# Revit family: 07101_CAI
name_source: partatom
category: Air Terminals
revit_build: Autodesk Revit MEP 2012 (Build: 20110309_2315(x64)
units: mm (PartAtom-declared; Revit-internal decimal feet)

## types (8) — shared parameters
Conect_Horizontal = 23 7/8"
Description = Difusor lineal para inyección
Función = Inyección
Longitud Mín.-Máx. = 24" (0.61 m) a 157 1/2" (4.0 m) en una sola pieza.
Manufacturer = INNES
Material = Aluminio
Medida_Requerida = 24"
Model = CAI
Nota1 = .
Nota_2 = .
Nota_3 = .
Posición de Instalación = Muro/Techo
Ranuras Disponibles = 1 a 8 ranuras
Separación entre Ranuras = 1/2", 3/4" ó 1"
Tipo de Cuello = Rectangular
Type Comments = Patrón de aire ajustable
URL = https://www.innes.com.mx
Visible_Texto1 = No
Visible_Texto2 = No
Visible_Texto3 = No

## per-type parameters (varying)
| type | Conect_Vertical | Nº_Ranuras | Separacion_Ranura | Var1 | Var2 |
| CAI_1-Ranura | 1 7/16" | 1 | 1/2" | 1 | 1/2" |
| CAI_2-Ranuras | 3 3/16" | 2 | 3/4" | 2 | 3/4" |
| CAI_3-Ranuras | 4 11/16" | 3 | 3/4" | 3 | 3/4" |
| CAI_4-Ranuras | 6 3/16" | 4 | 3/4" | 4 | 3/4" |
| CAI_5-Ranuras | 7 11/16" | 5 | 3/4" | 5 | 3/4" |
| CAI_6-Ranuras | 9 3/16" | 6 | 3/4" | 6 | 3/4" |
| CAI_7-Ranuras | 10 11/16" | 7 | 3/4" | 7 | 3/4" |
| CAI_8-Ranuras | 12 3/16" | 8 | 3/4" | 8 | 3/4" |

## geometry (parser evidence)
native form markers: Sweep x15
no freeform markers — native parametric forms only
